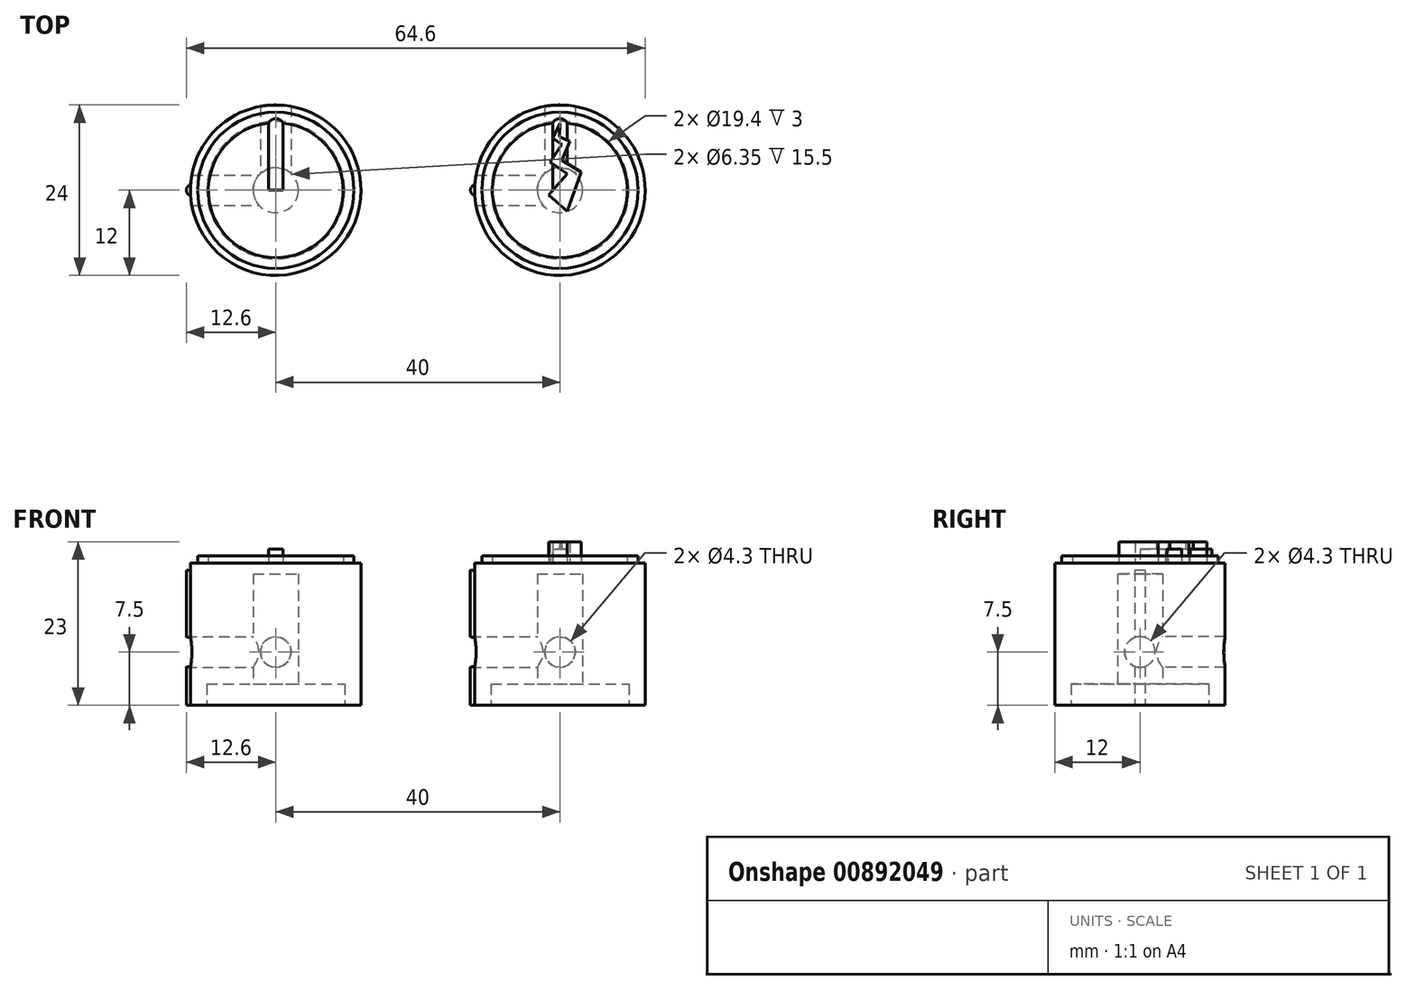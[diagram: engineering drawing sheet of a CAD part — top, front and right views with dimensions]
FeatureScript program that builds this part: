
annotation { "Feature Type Name" : "Feature", "Feature Type Description" : "" }
export const myFeature = defineFeature(function(context is Context, id is Id, definition is map)
    precondition{}
    {
        {
            var Q0;
            Q0=qCreatedBy(makeId("Top.planeOp"),FACE);
            var sketch = newSketch(context, id + "F0", { "sketchPlane" : qUnion([Q0])});
            skCircle(sketch, "E0", {"center": v(0, 0) * mm, "radius": 12 * mm});
            skSolve(sketch);
        }
        {
            var Q0;
            Q0 = qSketchRegion(id + "F0", true);
            extrude(context, id + "F1", {"entities" : qUnion([Q0]), "depth" : 20 * mm, "offsetDistance" : 25 * mm});
        }
        {
            var Q0;
            Q0=makeQuery(id+"F1.opExtrude","CAP_FACE",FACE,{"disambiguationData":[OSD([sQuery(id+"F0.wireOp",EDGE,"E0")])],"isStart":true});
            var sketch = newSketch(context, id + "F2", { "sketchPlane" : qUnion([Q0])});
            skCircle(sketch, "E1", {"center": v(0, 0) * mm, "radius": 9.7 * mm});
            skLineSegment(sketch, "E2", {"start": v(0, 9.7) * mm, "end": v(0, 12) * mm, "construction": true});
            skSolve(sketch);
        }
        {
            var Q0;
            Q0 = qSketchRegion(id + "F2", true);
            extrude(context, id + "F3", {"entities" : qUnion([Q0]), "operationType" : NewBodyOperationType.REMOVE, "oppositeDirection" : true, "depth" : 3 * mm, "offsetDistance" : 25 * mm});
        }
        {
            var Q0;
            Q0=makeQuery(id+"F3.boolean.opBoolean","COPY",FACE,{"derivedFrom":makeQuery(id+"F3.opExtrude","CAP_FACE",FACE,{"disambiguationData":[OSD([sQuery(id+"F2.wireOp",EDGE,"E1")])],"isStart":false})});
            var sketch = newSketch(context, id + "F4", { "sketchPlane" : qUnion([Q0])});
            skCircle(sketch, "E3", {"center": v(0, 0) * mm, "radius": 3.17 * mm});
            skSolve(sketch);
        }
        {
            var Q0;
            Q0 = qSketchRegion(id + "F4", true);
            extrude(context, id + "F5", {"entities" : qUnion([Q0]), "operationType" : NewBodyOperationType.REMOVE, "oppositeDirection" : true, "depth" : 15.5 * mm, "offsetDistance" : 25 * mm});
        }
        {
            var Q0;
            Q0=qCreatedBy(makeId("Front.planeOp"),FACE);
            var sketch = newSketch(context, id + "F6", { "sketchPlane" : qUnion([Q0])});
            skCircle(sketch, "E4", {"center": v(0, 7.5) * mm, "radius": 2.15 * mm});
            skLineSegment(sketch, "E5", {"start": v(0, 0) * mm, "end": v(0, 7.5) * mm, "construction": true});
            skPoint(sketch, "E6.orphan", {"position": v(0, 15) * mm});
            skSolve(sketch);
        }
        {
            var Q0;
            Q0=qCreatedBy(makeId("Right.planeOp"),FACE);
            var sketch = newSketch(context, id + "F7", { "sketchPlane" : qUnion([Q0])});
            skCircle(sketch, "E7", {"center": v(0, 7.5) * mm, "radius": 2.15 * mm});
            skLineSegment(sketch, "E8", {"start": v(0, 0) * mm, "end": v(0, 7.5) * mm, "construction": true});
            skSolve(sketch);
        }
        {
            var Q0;
            Q0=makeQuery(id+"F1.opExtrude","CAP_FACE",FACE,{"disambiguationData":[OSD([sQuery(id+"F0.wireOp",EDGE,"E0")])],"isStart":false});
            var sketch = newSketch(context, id + "F8", { "sketchPlane" : qUnion([Q0])});
            skCircle(sketch, "E9", {"center": v(0, 0) * mm, "radius": 11 * mm});
            skCircle(sketch, "E10", {"center": v(0, 0) * mm, "radius": 9.5 * mm});
            skLineSegment(sketch, "E11", {"start": v(-11, 0) * mm, "end": v(-9.5, 0) * mm, "construction": true});
            skLineSegment(sketch, "E12", {"start": v(-12, 0) * mm, "end": v(-11, 0) * mm, "construction": true});
            skSolve(sketch);
        }
        {
            var Q0;
            Q0=makeQuery(id+"F8.imprint","IMPRINT",FACE,{"disambiguationData":[TD([[makeQuery(id+"F8.imprint","IMPRINT",EDGE,{"derivedFrom":sQuery(id+"F8.wireOp",EDGE,"E9")}),1.0]])]});
            extrude(context, id + "F9", {"entities" : qUnion([Q0]), "operationType" : NewBodyOperationType.ADD, "depth" : 1 * mm, "offsetDistance" : 25 * mm});
        }
        {
            var Q0;
            Q0=makeQuery(id+"F9.boolean.opBoolean","SPLIT",FACE,{"disambiguationData":[TD([makeQuery(id+"F9.opExtrude","SWEPT_FACE",FACE,{"disambiguationData":[OSD([sQuery(id+"F8.wireOp",EDGE,"E10")])]})])],"derivedFrom":makeQuery(id+"F1.opExtrude","CAP_FACE",FACE,{"disambiguationData":[OSD([sQuery(id+"F0.wireOp",EDGE,"E0")])],"isStart":false})});
            var sketch = newSketch(context, id + "F10", { "sketchPlane" : qUnion([Q0])});
            skLineSegment(sketch, "E13", {"start": v(-1, 0) * mm, "end": v(0, 0) * mm});
            skLineSegment(sketch, "E14", {"start": v(0, 0) * mm, "end": v(1, 0) * mm});
            skLineSegment(sketch, "E15", {"start": v(1, 0) * mm, "end": v(1, 9.45) * mm});
            skLineSegment(sketch, "E16", {"start": v(-1, 9.45) * mm, "end": v(-1, 0) * mm});
            skArc(sketch, "E17", {"start": v(1, 9.45) * mm, "mid": v(0, 10.1) * mm, "end": v(-1, 9.45) * mm});
            skSolve(sketch);
        }
        {
            var Q0;
            Q0 = qSketchRegion(id + "F10", true);
            extrude(context, id + "F11", {"entities" : qUnion([Q0]), "operationType" : NewBodyOperationType.ADD, "depth" : 2 * mm, "offsetDistance" : 25 * mm});
        }
        {
            var Q0;
            Q0=qCreatedBy(makeId("Top.planeOp"),FACE);
            var sketch = newSketch(context, id + "F12", { "sketchPlane" : qUnion([Q0])});
            skArc(sketch, "E18", {"start": v(-11.97, 0.74) * mm, "mid": v(-12.6, 0) * mm, "end": v(-11.97, -0.72) * mm});
            skLineSegment(sketch, "E19", {"start": v(-11.97, 0.74) * mm, "end": v(-11.97, -0.72) * mm});
            skSolve(sketch);
        }
        {
            var Q0;
            Q0 = qSketchRegion(id + "F12", true);
            var Q1;
            {var subQ0=sQuery(id+"F0.wireOp",EDGE,"E0");Q1=makeQuery(id+"F9.boolean.opBoolean","SPLIT",FACE,{"disambiguationData":[TD([makeQuery(id+"F1.opExtrude","SWEPT_FACE",FACE,{"disambiguationData":[OSD([subQ0])]})])],"derivedFrom":makeQuery(id+"F1.opExtrude","CAP_FACE",FACE,{"disambiguationData":[OSD([subQ0])],"isStart":false})});}
            extrude(context, id + "F13", {"entities" : qUnion([Q0]), "operationType" : NewBodyOperationType.ADD, "endBound" : BoundingType.UP_TO_SURFACE, "depth" : 25 * mm, "endBoundEntityFace" : qUnion([Q1]), "hasOffset" : true, "offsetDistance" : 1 * mm});
        }
        {
            var Q0;
            Q0 = qSketchRegion(id + "F7", true);
            extrude(context, id + "F14", {"entities" : qUnion([Q0]), "operationType" : NewBodyOperationType.REMOVE, "oppositeDirection" : true, "depth" : 25 * mm, "offsetDistance" : 25 * mm});
        }
        {
            var Q0;
            Q0 = qSketchRegion(id + "F6", true);
            extrude(context, id + "F15", {"entities" : qUnion([Q0]), "operationType" : NewBodyOperationType.REMOVE, "oppositeDirection" : true, "depth" : 25 * mm, "offsetDistance" : 25 * mm});
        }
        {
            var Q0;
            Q0=makeQuery(id+"F1.opExtrude","SWEPT_BODY",BODY,{"disambiguationData":[OSD([sQuery(id+"F0.wireOp",EDGE,"E0")])]});
            transform(context, id + "F16", {"entities" : qUnion([Q0]), "transformType" : TransformType.TRANSLATION_3D, "dx" : 40 * mm, "dy" : 0 * mm, "dz" : 0 * mm, "makeCopy" : true});
        }
        {
            var Q0;
            Q0=makeQuery(id+"F16.opPattern","COPY",FACE,{"derivedFrom":makeQuery(id+"F9.boolean.opBoolean","SPLIT",FACE,{"disambiguationData":[TD([makeQuery(id+"F9.opExtrude","SWEPT_FACE",FACE,{"disambiguationData":[OSD([sQuery(id+"F8.wireOp",EDGE,"E10")])]})])],"derivedFrom":makeQuery(id+"F1.opExtrude","CAP_FACE",FACE,{"disambiguationData":[OSD([sQuery(id+"F0.wireOp",EDGE,"E0")])],"isStart":false})}),"instanceName":"1"});
            var sketch = newSketch(context, id + "F17", { "sketchPlane" : qUnion([Q0])});
            skLineSegment(sketch, "E20", {"start": v(39, 9.45) * mm, "end": v(41, 9.45) * mm, "construction": true});
            skLineSegment(sketch, "E21", {"start": v(40, 9.45) * mm, "end": v(39, 7.3) * mm});
            skLineSegment(sketch, "E22", {"start": v(39, 7.3) * mm, "end": v(40.3, 6.41) * mm});
            skLineSegment(sketch, "E23", {"start": v(40.3, 6.41) * mm, "end": v(38.6, 3.95) * mm});
            skLineSegment(sketch, "E24", {"start": v(38.6, 3.95) * mm, "end": v(41, 2.29) * mm});
            skLineSegment(sketch, "E25", {"start": v(41, 2.29) * mm, "end": v(38.41, -0.7) * mm});
            skLineSegment(sketch, "E26", {"start": v(38.41, -0.7) * mm, "end": v(41, -2.94) * mm});
            skLineSegment(sketch, "E27", {"start": v(41, -2.94) * mm, "end": v(43.01, 2.58) * mm});
            skLineSegment(sketch, "E28", {"start": v(43.01, 2.58) * mm, "end": v(40.3, 4.21) * mm});
            skLineSegment(sketch, "E29", {"start": v(40.3, 4.21) * mm, "end": v(41.42, 6.87) * mm});
            skLineSegment(sketch, "E30", {"start": v(41.42, 6.87) * mm, "end": v(39.94, 7.5) * mm});
            skLineSegment(sketch, "E31", {"start": v(39.94, 7.5) * mm, "end": v(40, 9.45) * mm});
            skSolve(sketch);
        }
        {
            var Q0;
            Q0 = qSketchRegion(id + "F17", true);
            extrude(context, id + "F18", {"entities" : qUnion([Q0]), "operationType" : NewBodyOperationType.ADD, "depth" : 3 * mm, "offsetDistance" : 25 * mm});
        }
    });
